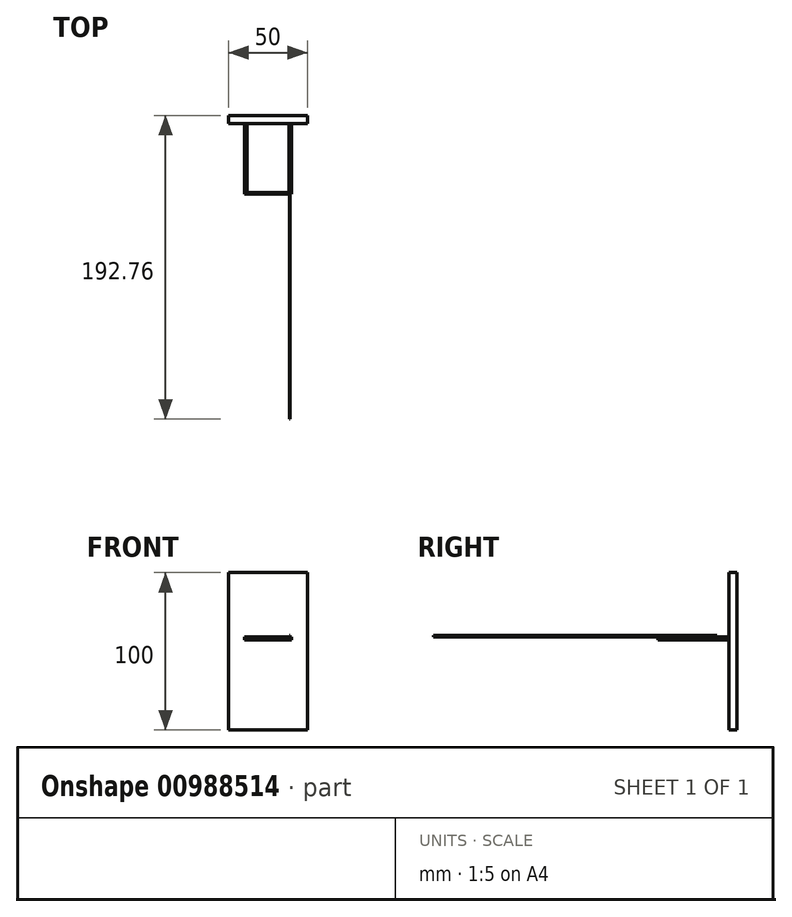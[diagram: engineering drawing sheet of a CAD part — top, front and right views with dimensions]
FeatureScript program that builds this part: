
annotation { "Feature Type Name" : "Feature", "Feature Type Description" : "" }
export const myFeature = defineFeature(function(context is Context, id is Id, definition is map)
    precondition{}
    {
        {
            var Q0;
            Q0=qCreatedBy(makeId("Front.planeOp"),FACE);
            var sketch = newSketch(context, id + "F0", { "sketchPlane" : qUnion([Q0])});
            skLineSegment(sketch, "E0.bottom", {"start": v(-35.97, 40.88) * mm, "end": v(14.03, 40.88) * mm});
            skLineSegment(sketch, "E0.top", {"start": v(-35.97, -59.12) * mm, "end": v(14.03, -59.12) * mm});
            skLineSegment(sketch, "E0.left", {"start": v(-35.97, 40.88) * mm, "end": v(-35.97, -59.12) * mm});
            skLineSegment(sketch, "E0.right", {"start": v(14.03, 40.88) * mm, "end": v(14.03, -59.12) * mm});
            skSolve(sketch);
        }
        {
            var Q0;
            Q0=makeQuery(id+"F0.imprint","IMPRINT",FACE,{"disambiguationData":[TD([[makeQuery(id+"F0.imprint","IMPRINT",EDGE,{"derivedFrom":sQuery(id+"F0.wireOp",EDGE,"E0.bottom")}),-1.0]])]});
            extrude(context, id + "F1", {"entities" : qUnion([Q0]), "depth" : 5 * mm, "offsetDistance" : 25 * mm});
        }
        {
            var Q0;
            Q0=makeQuery(id+"F1.opExtrude","CAP_FACE",FACE,{"disambiguationData":[OSD([sQuery(id+"F0.wireOp",EDGE,"E0.bottom"),sQuery(id+"F0.wireOp",EDGE,"E0.top"),sQuery(id+"F0.wireOp",EDGE,"E0.left"),sQuery(id+"F0.wireOp",EDGE,"E0.right")])],"isStart":false});
            var sketch = newSketch(context, id + "F2", { "sketchPlane" : qUnion([Q0])});
            skLineSegment(sketch, "E1.bottom", {"start": v(-25.97, 0) * mm, "end": v(4.03, 0) * mm});
            skLineSegment(sketch, "E1.top", {"start": v(-25.97, -2) * mm, "end": v(4.03, -2) * mm});
            skLineSegment(sketch, "E1.left", {"start": v(-25.97, 0) * mm, "end": v(-25.97, -2) * mm});
            skLineSegment(sketch, "E1.right", {"start": v(4.03, 0) * mm, "end": v(4.03, -2) * mm});
            skSolve(sketch);
        }
        {
            var Q0;
            Q0=makeQuery(id+"F2.imprint","IMPRINT",FACE,{"disambiguationData":[TD([[makeQuery(id+"F2.imprint","IMPRINT",EDGE,{"derivedFrom":sQuery(id+"F2.wireOp",EDGE,"E1.bottom")}),-1.0]])]});
            extrude(context, id + "F3", {"entities" : qUnion([Q0]), "operationType" : NewBodyOperationType.ADD, "depth" : 45 * mm, "offsetDistance" : 25 * mm});
        }
        {
            var Q0;
            Q0=makeQuery(id+"F3.opExtrude","SWEPT_FACE",FACE,{"disambiguationData":[OSD([sQuery(id+"F2.wireOp",EDGE,"E1.top")])]});
            var sketch = newSketch(context, id + "F4", { "sketchPlane" : qUnion([Q0])});
            skLineSegment(sketch, "E2.bottom", {"start": v(-21.97, 5) * mm, "end": v(0, 5) * mm});
            skLineSegment(sketch, "E3.bottom", {"start": v(-24.38, 5) * mm, "end": v(2.36, 5) * mm});
            skLineSegment(sketch, "E3.top", {"start": v(-24.38, 48.89) * mm, "end": v(2.36, 48.89) * mm});
            skLineSegment(sketch, "E3.left", {"start": v(-24.38, 5) * mm, "end": v(-24.38, 48.89) * mm});
            skLineSegment(sketch, "E3.right", {"start": v(2.36, 5) * mm, "end": v(2.36, 48.89) * mm});
            skSolve(sketch);
        }
        {
            var Q0;
            Q0=makeQuery(id+"F4.imprint","IMPRINT",FACE,{"disambiguationData":[TD([[makeQuery(id+"F4.imprint","IMPRINT",EDGE,{"derivedFrom":sQuery(id+"F4.wireOp",EDGE,"E3.top")}),-1.0]])]});
            extrude(context, id + "F5", {"entities" : qUnion([Q0]), "operationType" : NewBodyOperationType.REMOVE, "oppositeDirection" : true, "depth" : 41 * mm, "offsetDistance" : 25 * mm});
        }
        {
            var Q0;
            Q0=makeQuery(id+"F3.opExtrude","SWEPT_FACE",FACE,{"disambiguationData":[OSD([sQuery(id+"F2.wireOp",EDGE,"E1.bottom")])]});
            var sketch = newSketch(context, id + "F6", { "sketchPlane" : qUnion([Q0])});
            skLineSegment(sketch, "E4.bottom", {"start": v(2.62, -12.76) * mm, "end": v(3.1, -12.76) * mm});
            skLineSegment(sketch, "E4.top", {"start": v(2.62, -162.76) * mm, "end": v(3.1, -162.76) * mm});
            skLineSegment(sketch, "E4.left", {"start": v(2.62, -12.76) * mm, "end": v(2.62, -162.76) * mm});
            skLineSegment(sketch, "E4.right", {"start": v(3.1, -12.76) * mm, "end": v(3.1, -162.76) * mm});
            skSolve(sketch);
        }
        {
            var Q0;
            {var subQ0=sQuery(id+"F6.wireOp",EDGE,"E4.top");Q0=makeQuery(id+"F6.imprint","IMPRINT",FACE,{"disambiguationData":[TD([[makeQuery(id+"F6.imprint","IMPRINT",EDGE,{"derivedFrom":subQ0}),1.0]])]});}
            var Q1;
            {var subQ0=sQuery(id+"F6.wireOp",EDGE,"E4.bottom");Q1=makeQuery(id+"F6.imprint","IMPRINT",FACE,{"disambiguationData":[TD([[makeQuery(id+"F6.imprint","IMPRINT",EDGE,{"derivedFrom":subQ0}),-1.0]])]});}
            extrude(context, id + "F7", {"entities" : qUnion([Q0, Q1]), "operationType" : NewBodyOperationType.ADD, "depth" : 1 * mm, "offsetDistance" : 25 * mm});
        }
        {
            var Q0;
            Q0=makeQuery(id+"F7.opExtrude","SWEPT_FACE",FACE,{"disambiguationData":[OSD([sQuery(id+"F6.wireOp",EDGE,"E4.top")])]});
            extrude(context, id + "F8", {"entities" : qUnion([Q0]), "operationType" : NewBodyOperationType.ADD, "depth" : 30 * mm, "offsetDistance" : 25 * mm});
        }
    });
